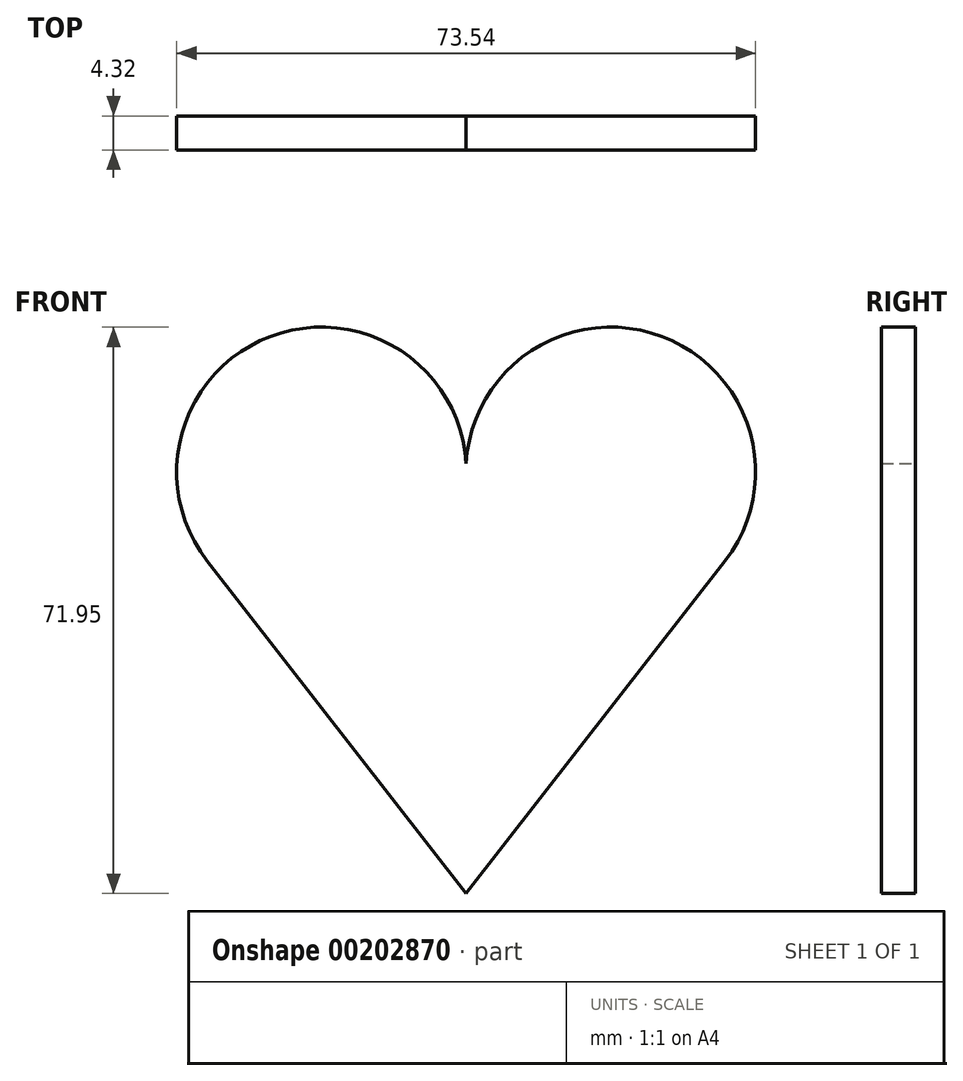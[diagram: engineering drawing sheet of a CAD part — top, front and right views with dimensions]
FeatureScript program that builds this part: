
annotation { "Feature Type Name" : "Feature", "Feature Type Description" : "" }
export const myFeature = defineFeature(function(context is Context, id is Id, definition is map)
    precondition{}
    {
        {
            var Q0;
            Q0=qCreatedBy(makeId("Front.planeOp"),FACE);
            var sketch = newSketch(context, id + "F0", { "sketchPlane" : qUnion([Q0])});
            skArc(sketch, "E0", {"start": v(32.89, 6.9) * mm, "mid": v(24.85, 35.41) * mm, "end": v(0, 19.27) * mm});
            skLineSegment(sketch, "E1", {"start": v(0, 19.27) * mm, "end": v(0, -35.36) * mm});
            skLineSegment(sketch, "E2", {"start": v(0, -35.36) * mm, "end": v(32.89, 6.9) * mm});
            skArc(sketch, "E3.MirrorCS", {"start": v(-32.89, 6.9) * mm, "mid": v(-24.85, 35.41) * mm, "end": v(0, 19.27) * mm});
            skLineSegment(sketch, "E4.MirrorCS", {"start": v(0, -35.36) * mm, "end": v(-32.89, 6.9) * mm});
            skSolve(sketch);
        }
        {
            var Q0;
            Q0=makeQuery(id+"F0.imprint","IMPRINT",FACE,{"disambiguationData":[TD([[makeQuery(id+"F0.imprint","IMPRINT",EDGE,{"derivedFrom":sQuery(id+"F0.wireOp",EDGE,"E1")}),-1.0]])]});
            var Q1;
            Q1=makeQuery(id+"F0.imprint","IMPRINT",FACE,{"disambiguationData":[TD([[makeQuery(id+"F0.imprint","IMPRINT",EDGE,{"derivedFrom":sQuery(id+"F0.wireOp",EDGE,"E0")}),1.0]])]});
            extrude(context, id + "F1", {"entities" : qUnion([Q0, Q1]), "depth" : 4.32 * mm});
        }
    });
